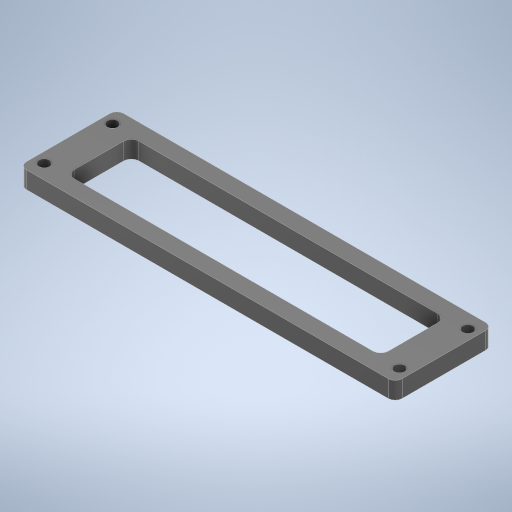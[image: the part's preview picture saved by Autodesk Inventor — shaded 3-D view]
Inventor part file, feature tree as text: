
AUTODESK INVENTOR PART (.ipt)
format: ipt  version: 2024.2 (Build 282272000, 272)  size: 288,768 bytes
history: native  units: mm
features: sketch x2, other x1, extrude x1, hole x1
ambient origin geometry x8: Origin, YZ Plane, XZ Plane, XY Plane, X Axis, Y Axis, Z Axis, Center Point
bodies: Solid1 (feature_tree)
feature tree (5):
  other  "TorsoButtonUpperCoverFrame.ipt"
  sketch  "Sketch3"  dims[d2=3.0mm d4=5.0mm d5=0.0mm d6=3.2mm d7=6.0mm d8=4.0mm d9=2.0mm d10=90.0deg d11=8.0mm d12=20.594885mm]
  extrude  "Extrusion1"  Depth=10.0mm
  hole  "Phi3.2"  [1 undecoded]
  sketch  "Sketch2"  dims[d0=10.0mm d1=3.0mm]
note: 1 required parameter value undecoded (feature->parameter linkage not recoverable at this tier; creation-order binding heuristic only, values carry confidence <= 0.55)
